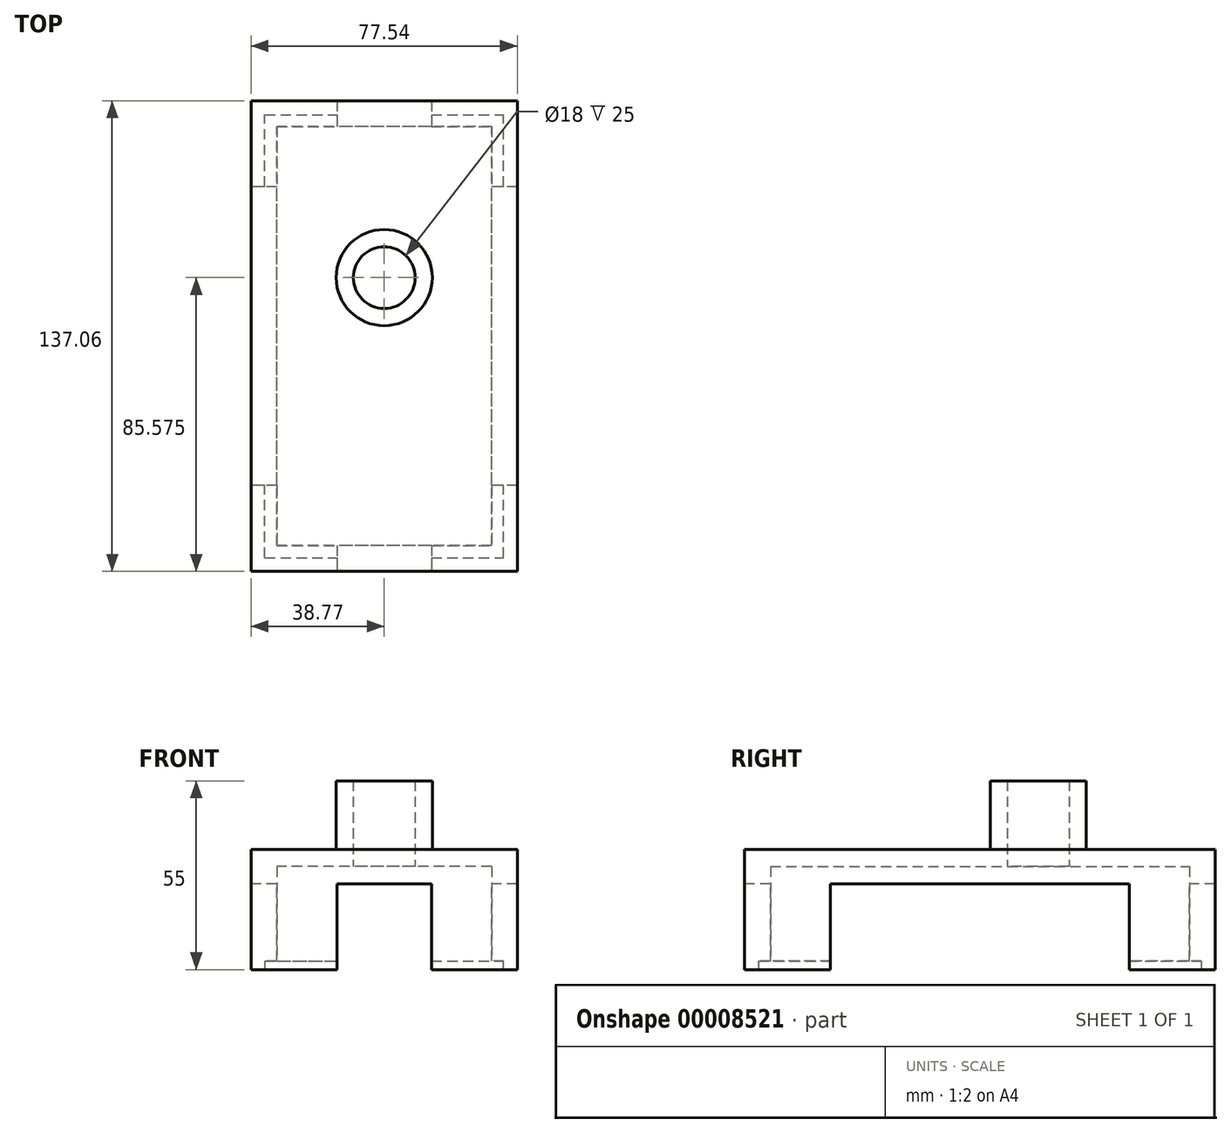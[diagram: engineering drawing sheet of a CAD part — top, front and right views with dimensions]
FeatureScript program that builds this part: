
annotation { "Feature Type Name" : "Feature", "Feature Type Description" : "" }
export const myFeature = defineFeature(function(context is Context, id is Id, definition is map)
    precondition{}
    {
        {
            var Q0;
            Q0=qCreatedBy(makeId("Top.planeOp"),FACE);
            var sketch = newSketch(context, id + "F0", { "sketchPlane" : qUnion([Q0])});
            skLineSegment(sketch, "E0.rect.bottom", {"start": v(38.78, -68.53) * mm, "end": v(-38.78, -68.53) * mm});
            skLineSegment(sketch, "E0.rect.top", {"start": v(38.77, 68.53) * mm, "end": v(-38.78, 68.53) * mm});
            skLineSegment(sketch, "E0.rect.left", {"start": v(38.78, -68.53) * mm, "end": v(38.78, 68.53) * mm});
            skLineSegment(sketch, "E0.rect.right", {"start": v(-38.77, -68.53) * mm, "end": v(-38.78, 68.53) * mm});
            skPoint(sketch, "E0.rect.middle", {"position": v(0, 0) * mm});
            skLineSegment(sketch, "E1.rect.bottom", {"start": v(31.28, -61.03) * mm, "end": v(-31.28, -61.03) * mm});
            skLineSegment(sketch, "E1.rect.top", {"start": v(31.28, 61.03) * mm, "end": v(-31.28, 61.03) * mm});
            skLineSegment(sketch, "E1.rect.left", {"start": v(31.28, -61.03) * mm, "end": v(31.28, 61.03) * mm});
            skLineSegment(sketch, "E1.rect.right", {"start": v(-31.28, -61.03) * mm, "end": v(-31.28, 61.03) * mm});
            skSolve(sketch);
        }
        {
            var Q0;
            Q0=makeQuery(id+"F0.imprint","IMPRINT",FACE,{"disambiguationData":[TD([[makeQuery(id+"F0.imprint","IMPRINT",EDGE,{"derivedFrom":sQuery(id+"F0.wireOp",EDGE,"E0.rect.bottom")}),-1.0]])]});
            extrude(context, id + "F1", {"entities" : qUnion([Q0]), "depth" : 30 * mm});
        }
        {
            var Q0;
            Q0=makeQuery(id+"F1.opExtrude","CAP_FACE",FACE,{"disambiguationData":[OSD([sQuery(id+"F0.wireOp",EDGE,"E0.rect.bottom"),sQuery(id+"F0.wireOp",EDGE,"E0.rect.top"),sQuery(id+"F0.wireOp",EDGE,"E0.rect.left"),sQuery(id+"F0.wireOp",EDGE,"E0.rect.right"),sQuery(id+"F0.wireOp",EDGE,"E1.rect.bottom"),sQuery(id+"F0.wireOp",EDGE,"E1.rect.top"),sQuery(id+"F0.wireOp",EDGE,"E1.rect.left"),sQuery(id+"F0.wireOp",EDGE,"E1.rect.right")])],"isStart":false});
            var sketch = newSketch(context, id + "F2", { "sketchPlane" : qUnion([Q0])});
            skLineSegment(sketch, "E2.rect.bottom", {"start": v(-38.77, -68.53) * mm, "end": v(38.77, -68.53) * mm});
            skLineSegment(sketch, "E2.rect.top", {"start": v(-38.77, 68.53) * mm, "end": v(38.77, 68.53) * mm});
            skLineSegment(sketch, "E2.rect.left", {"start": v(-38.77, -68.53) * mm, "end": v(-38.77, 68.53) * mm});
            skLineSegment(sketch, "E2.rect.right", {"start": v(38.77, -68.53) * mm, "end": v(38.77, 68.53) * mm});
            skPoint(sketch, "E2.rect.middle", {"position": v(0, 0) * mm});
            skCircle(sketch, "E3", {"center": v(0, 17.05) * mm, "radius": 9 * mm});
            skSolve(sketch);
        }
        {
            var Q0;
            Q0=makeQuery(id+"F2.imprint","IMPRINT",FACE,{"disambiguationData":[TD([[makeQuery(id+"F2.imprint","IMPRINT",EDGE,{"derivedFrom":sQuery(id+"F2.wireOp",EDGE,"E3")}),-1.0]])]});
            var Q1;
            Q1=makeQuery(id+"F2.imprint","IMPRINT",FACE,{"disambiguationData":[TD([[makeQuery(id+"F2.imprint","IMPRINT",EDGE,{"derivedFrom":sQuery(id+"F2.wireOp",EDGE,"E2.rect.bottom")}),-1.0]])]});
            extrude(context, id + "F3", {"entities" : qUnion([Q0, Q1]), "operationType" : NewBodyOperationType.ADD, "depth" : 5 * mm});
        }
        {
            var Q0;
            Q0=makeQuery(id+"F3.opExtrude","CAP_FACE",FACE,{"disambiguationData":[OSD([sQuery(id+"F2.wireOp",EDGE,"E2.rect.bottom"),sQuery(id+"F2.wireOp",EDGE,"E2.rect.top"),sQuery(id+"F2.wireOp",EDGE,"E2.rect.left"),sQuery(id+"F2.wireOp",EDGE,"E2.rect.right"),sQuery(id+"F2.wireOp",EDGE,"fe69ce92-d596-438b-8a41-674941515217")])],"isStart":false});
            var sketch = newSketch(context, id + "F4", { "sketchPlane" : qUnion([Q0])});
            skCircle(sketch, "E4.0", {"center": v(0, 17.05) * mm, "radius": 9 * mm});
            skCircle(sketch, "E5", {"center": v(0, 17.05) * mm, "radius": 14 * mm});
            skSolve(sketch);
        }
        {
            var Q0;
            Q0 = qSketchRegion(id + "F4", true);
            extrude(context, id + "F5", {"entities" : qUnion([Q0]), "operationType" : NewBodyOperationType.ADD, "depth" : 20 * mm});
        }
        {
            var Q0;
            Q0=makeQuery(id+"F1.opExtrude","CAP_FACE",FACE,{"disambiguationData":[OSD([sQuery(id+"F0.wireOp",EDGE,"E0.rect.bottom"),sQuery(id+"F0.wireOp",EDGE,"E0.rect.top"),sQuery(id+"F0.wireOp",EDGE,"E0.rect.left"),sQuery(id+"F0.wireOp",EDGE,"E0.rect.right"),sQuery(id+"F0.wireOp",EDGE,"E1.rect.bottom"),sQuery(id+"F0.wireOp",EDGE,"E1.rect.top"),sQuery(id+"F0.wireOp",EDGE,"E1.rect.left"),sQuery(id+"F0.wireOp",EDGE,"E1.rect.right")])],"isStart":true});
            var sketch = newSketch(context, id + "F6", { "sketchPlane" : qUnion([Q0])});
            skLineSegment(sketch, "E6.bottom", {"start": v(-34.78, 64.53) * mm, "end": v(34.77, 64.53) * mm});
            skLineSegment(sketch, "E6.top", {"start": v(-34.78, -64.53) * mm, "end": v(34.78, -64.53) * mm});
            skLineSegment(sketch, "E6.left", {"start": v(-34.78, 64.53) * mm, "end": v(-34.78, -64.53) * mm});
            skLineSegment(sketch, "E6.right", {"start": v(34.77, 64.53) * mm, "end": v(34.78, -64.53) * mm});
            skSolve(sketch);
        }
        {
            var Q0;
            Q0 = qSketchRegion(id + "F6", true);
            extrude(context, id + "F7", {"entities" : qUnion([Q0]), "operationType" : NewBodyOperationType.REMOVE, "oppositeDirection" : true, "depth" : 2.5 * mm});
        }
        {
            var Q0;
            Q0=qCreatedBy(makeId("Top.planeOp"),FACE);
            var sketch = newSketch(context, id + "F8", { "sketchPlane" : qUnion([Q0])});
            skLineSegment(sketch, "E7.bottom", {"start": v(50.09, 43.53) * mm, "end": v(-50.36, 43.53) * mm});
            skLineSegment(sketch, "E7.top", {"start": v(50.09, -43.53) * mm, "end": v(-50.36, -43.53) * mm});
            skLineSegment(sketch, "E7.left", {"start": v(50.09, 43.53) * mm, "end": v(50.09, -43.53) * mm});
            skLineSegment(sketch, "E7.right", {"start": v(-50.36, 43.53) * mm, "end": v(-50.36, -43.53) * mm});
            skLineSegment(sketch, "E8.bottom", {"start": v(13.77, 75.07) * mm, "end": v(-13.78, 75.07) * mm});
            skLineSegment(sketch, "E8.top", {"start": v(13.78, -77.3) * mm, "end": v(-13.77, -77.3) * mm});
            skLineSegment(sketch, "E8.left", {"start": v(13.77, 75.07) * mm, "end": v(13.78, -77.3) * mm});
            skLineSegment(sketch, "E8.right", {"start": v(-13.78, 75.07) * mm, "end": v(-13.77, -77.3) * mm});
            skSolve(sketch);
        }
        {
            var Q0;
            Q0 = qSketchRegion(id + "F8", true);
            extrude(context, id + "F9", {"entities" : qUnion([Q0]), "operationType" : NewBodyOperationType.REMOVE, "depth" : 25 * mm});
        }
    });
